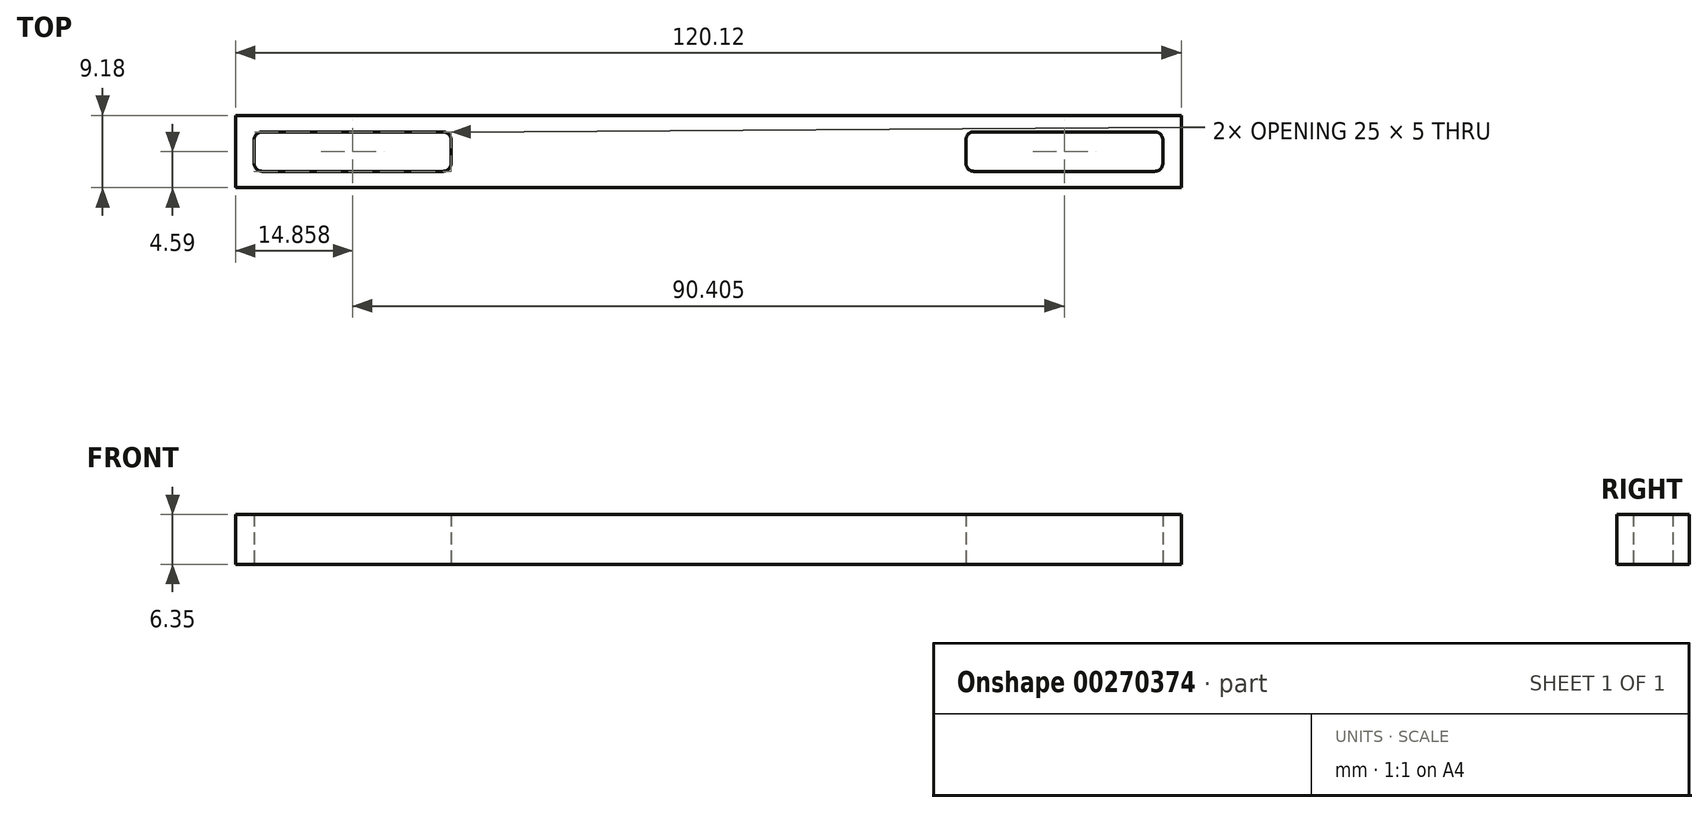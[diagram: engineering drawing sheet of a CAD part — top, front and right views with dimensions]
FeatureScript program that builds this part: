
annotation { "Feature Type Name" : "Feature", "Feature Type Description" : "" }
export const myFeature = defineFeature(function(context is Context, id is Id, definition is map)
    precondition{}
    {
        {
            var Q0;
            Q0=qCreatedBy(makeId("Top.planeOp"),FACE);
            var sketch = newSketch(context, id + "F0", { "sketchPlane" : qUnion([Q0])});
            skLineSegment(sketch, "E0.bottom", {"start": v(60.06, -4.6) * mm, "end": v(-60.06, -4.6) * mm});
            skLineSegment(sketch, "E0.top", {"start": v(60.06, 4.6) * mm, "end": v(-60.06, 4.6) * mm});
            skLineSegment(sketch, "E0.left", {"start": v(60.06, -4.6) * mm, "end": v(60.06, 4.6) * mm});
            skLineSegment(sketch, "E0.right", {"start": v(-60.06, -4.6) * mm, "end": v(-60.06, 4.6) * mm});
            skPoint(sketch, "E0.middle", {"position": v(0, 0) * mm});
            skLineSegment(sketch, "E1.bottom", {"start": v(-32.7, -2.5) * mm, "end": v(-57.7, -2.5) * mm});
            skLineSegment(sketch, "E1.top", {"start": v(-32.7, 2.5) * mm, "end": v(-57.7, 2.5) * mm});
            skLineSegment(sketch, "E1.left", {"start": v(-32.7, -2.5) * mm, "end": v(-32.7, 2.5) * mm});
            skLineSegment(sketch, "E1.right", {"start": v(-57.7, -2.5) * mm, "end": v(-57.7, 2.5) * mm});
            skPoint(sketch, "E1.middle", {"position": v(-45.2, 0) * mm});
            skLineSegment(sketch, "E2.MirrorCS", {"start": v(32.7, -2.5) * mm, "end": v(32.7, 2.5) * mm});
            skLineSegment(sketch, "E3.MirrorCS", {"start": v(32.7, 2.5) * mm, "end": v(57.7, 2.5) * mm});
            skLineSegment(sketch, "E4.MirrorCS", {"start": v(32.7, -2.5) * mm, "end": v(57.7, -2.5) * mm});
            skLineSegment(sketch, "E5.MirrorCS", {"start": v(57.7, -2.5) * mm, "end": v(57.7, 2.5) * mm});
            skSolve(sketch);
        }
        {
            var Q0;
            Q0 = qSketchRegion(id + "F0", true);
            extrude(context, id + "F1", {"entities" : qUnion([Q0]), "depth" : 6.35 * mm});
        }
        {
            var Q0;
            Q0=makeQuery(id+"F1.opExtrude","SWEPT_EDGE",EDGE,{"disambiguationData":[OSD([sQuery(id+"F0.wireOp",EDGE,"E1.top"),sQuery(id+"F0.wireOp",EDGE,"E1.right")])]});
            var Q1;
            Q1=makeQuery(id+"F1.opExtrude","SWEPT_EDGE",EDGE,{"disambiguationData":[OSD([sQuery(id+"F0.wireOp",EDGE,"E1.bottom"),sQuery(id+"F0.wireOp",EDGE,"E1.right")])]});
            var Q2;
            Q2=makeQuery(id+"F1.opExtrude","SWEPT_EDGE",EDGE,{"disambiguationData":[OSD([sQuery(id+"F0.wireOp",EDGE,"E3.MirrorCS"),sQuery(id+"F0.wireOp",EDGE,"E5.MirrorCS")])]});
            var Q3;
            Q3=makeQuery(id+"F1.opExtrude","SWEPT_EDGE",EDGE,{"disambiguationData":[OSD([sQuery(id+"F0.wireOp",EDGE,"E4.MirrorCS"),sQuery(id+"F0.wireOp",EDGE,"E5.MirrorCS")])]});
            var Q4;
            Q4=makeQuery(id+"F1.opExtrude","SWEPT_EDGE",EDGE,{"disambiguationData":[OSD([sQuery(id+"F0.wireOp",EDGE,"E2.MirrorCS"),sQuery(id+"F0.wireOp",EDGE,"E4.MirrorCS")])]});
            var Q5;
            Q5=makeQuery(id+"F1.opExtrude","SWEPT_EDGE",EDGE,{"disambiguationData":[OSD([sQuery(id+"F0.wireOp",EDGE,"E2.MirrorCS"),sQuery(id+"F0.wireOp",EDGE,"E3.MirrorCS")])]});
            var Q6;
            Q6=makeQuery(id+"F1.opExtrude","SWEPT_EDGE",EDGE,{"disambiguationData":[OSD([sQuery(id+"F0.wireOp",EDGE,"E1.bottom"),sQuery(id+"F0.wireOp",EDGE,"E1.left")])]});
            var Q7;
            Q7=makeQuery(id+"F1.opExtrude","SWEPT_EDGE",EDGE,{"disambiguationData":[OSD([sQuery(id+"F0.wireOp",EDGE,"E1.top"),sQuery(id+"F0.wireOp",EDGE,"E1.left")])]});
            fillet(context, id + "F2", {"entities" : qUnion([Q0, Q1, Q2, Q3, Q4, Q5, Q6, Q7]), "radius" : 1 * mm, "tangentPropagation" : true, "allowEdgeOverflow" : false});
        }
    });
